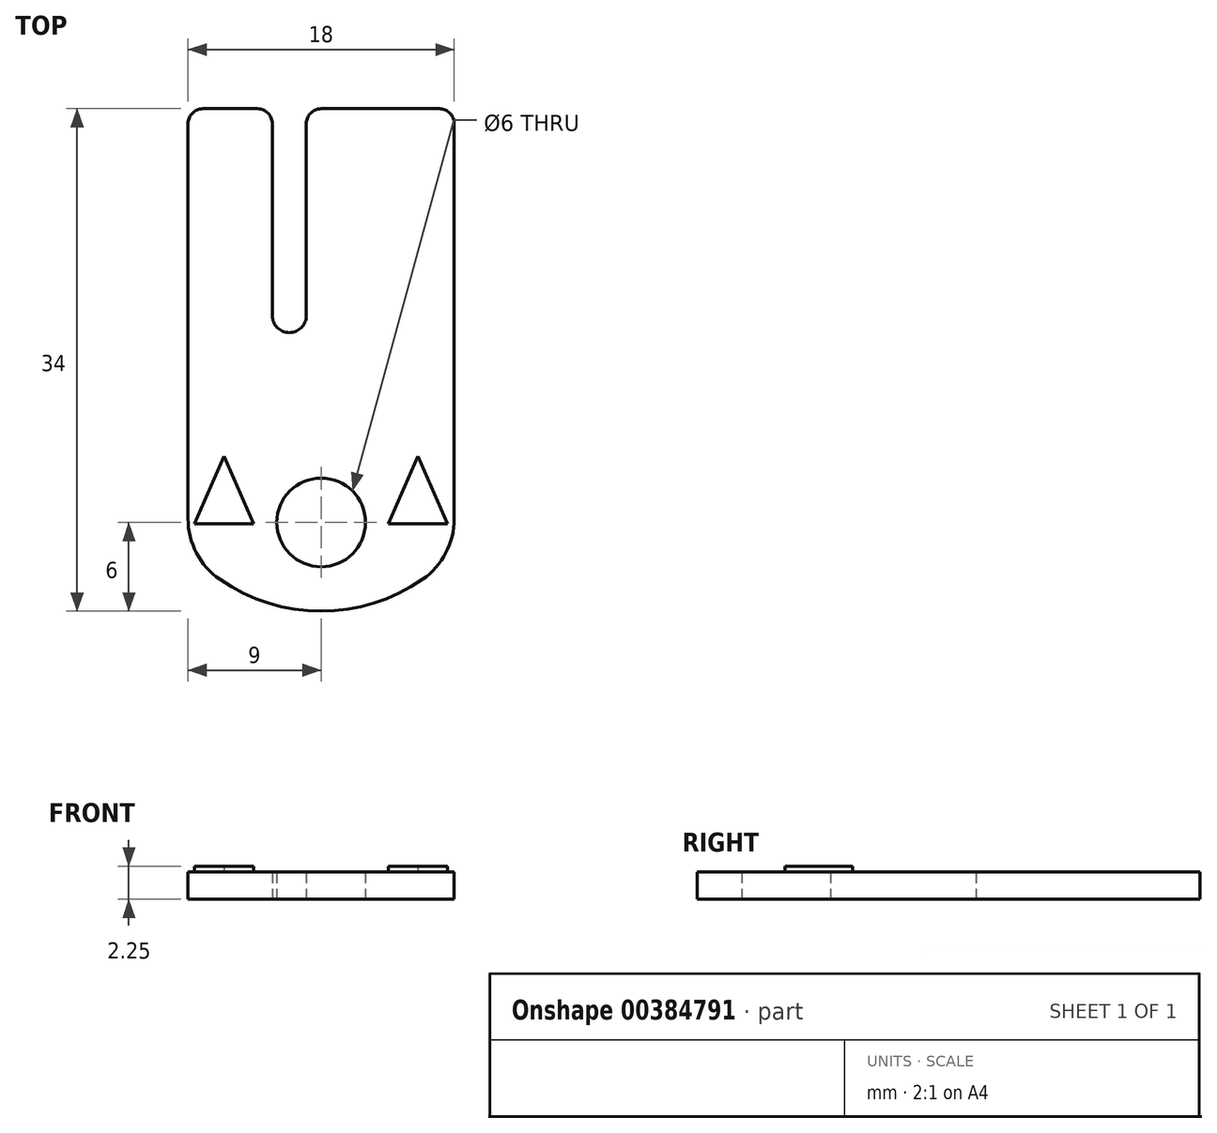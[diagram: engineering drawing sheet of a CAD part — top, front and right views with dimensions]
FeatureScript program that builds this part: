
annotation { "Feature Type Name" : "Feature", "Feature Type Description" : "" }
export const myFeature = defineFeature(function(context is Context, id is Id, definition is map)
    precondition{}
    {
        {
            var Q0;
            Q0=qCreatedBy(makeId("Top.planeOp"),FACE);
            var sketch = newSketch(context, id + "F0", { "sketchPlane" : qUnion([Q0])});
            skLineSegment(sketch, "E0.top", {"start": v(1, 22) * mm, "end": v(4.7, 22) * mm});
            skLineSegment(sketch, "E0.left", {"start": v(0, 1) * mm, "end": v(0, 21) * mm});
            skLineSegment(sketch, "E0.right", {"start": v(18, 1) * mm, "end": v(18, 21) * mm});
            skArc(sketch, "E1", {"start": v(2.14, -9.85) * mm, "mid": v(9, -12) * mm, "end": v(15.86, -9.85) * mm});
            skPoint(sketch, "E2.visualSharp", {"position": v(18, 22) * mm});
            skArc(sketch, "E2.filletArc", {"start": v(18, 21) * mm, "mid": v(17.7, 21.7) * mm, "end": v(17, 22) * mm});
            skPoint(sketch, "E3.visualSharp", {"position": v(0, 22) * mm});
            skArc(sketch, "E3.filletArc", {"start": v(1, 22) * mm, "mid": v(0.3, 21.7) * mm, "end": v(0, 21) * mm});
            skPoint(sketch, "E4.visualSharp", {"position": v(-3, 0) * mm});
            skPoint(sketch, "E5.visualSharp", {"position": v(21, 0) * mm});
            skPoint(sketch, "E6.visualSharp", {"position": v(18, 0) * mm});
            skPoint(sketch, "E7.visualSharp", {"position": v(0, 0) * mm});
            skLineSegment(sketch, "E8", {"start": v(5.7, 21) * mm, "end": v(5.7, 8) * mm});
            skLineSegment(sketch, "E9", {"start": v(8, 8) * mm, "end": v(8, 21) * mm});
            skArc(sketch, "E10", {"start": v(5.7, 8) * mm, "mid": v(6.85, 6.85) * mm, "end": v(8, 8) * mm});
            skLineSegment(sketch, "E11.trimOffspring", {"start": v(9, 22) * mm, "end": v(17, 22) * mm});
            skCircle(sketch, "E12", {"center": v(9, -6) * mm, "radius": 3 * mm});
            skPoint(sketch, "E12.centerSnap0", {"position": v(9, -12) * mm});
            skPoint(sketch, "E13.visualSharp", {"position": v(5.7, 22) * mm});
            skArc(sketch, "E13.filletArc", {"start": v(5.7, 21) * mm, "mid": v(5.4, 21.7) * mm, "end": v(4.7, 22) * mm});
            skPoint(sketch, "E14.visualSharp", {"position": v(8, 22) * mm});
            skArc(sketch, "E14.filletArc", {"start": v(9, 22) * mm, "mid": v(8.3, 21.7) * mm, "end": v(8, 21) * mm});
            skLineSegment(sketch, "E15", {"start": v(18, 1) * mm, "end": v(18, -5.74) * mm});
            skLineSegment(sketch, "E16", {"start": v(0, 1) * mm, "end": v(0, -5.74) * mm});
            skPoint(sketch, "E17.visualSharp", {"position": v(0, -7.94) * mm});
            skArc(sketch, "E17.filletArc", {"start": v(0, -5.74) * mm, "mid": v(0.57, -8.06) * mm, "end": v(2.14, -9.85) * mm});
            skPoint(sketch, "E18.visualSharp", {"position": v(18, -7.94) * mm});
            skArc(sketch, "E18.filletArc", {"start": v(15.86, -9.85) * mm, "mid": v(17.43, -8.06) * mm, "end": v(18, -5.74) * mm});
            skSolve(sketch);
        }
        {
            var Q0;
            Q0 = qSketchRegion(id + "F0", true);
            extrude(context, id + "F1", {"entities" : qUnion([Q0]), "depth" : 1.85 * mm});
        }
        {
            var Q0;
            Q0=makeQuery(id+"F1.opExtrude","CAP_FACE",FACE,{"disambiguationData":[OSD([sQuery(id+"F0.wireOp",EDGE,"E0.top"),sQuery(id+"F0.wireOp",EDGE,"E0.left"),sQuery(id+"F0.wireOp",EDGE,"E0.right"),sQuery(id+"F0.wireOp",EDGE,"E1"),sQuery(id+"F0.wireOp",EDGE,"HsPN8c6q-kJPd-bA8U-ZaCK-iASUxXpfGAAi"),sQuery(id+"F0.wireOp",EDGE,"Gjcc5HDl-sNZp-f0TE-VZhq-E6EV8sQHwBPA"),sQuery(id+"F0.wireOp",EDGE,"E2.filletArc"),sQuery(id+"F0.wireOp",EDGE,"E3.filletArc"),sQuery(id+"F0.wireOp",EDGE,"E4.filletArc"),sQuery(id+"F0.wireOp",EDGE,"E5.filletArc"),sQuery(id+"F0.wireOp",EDGE,"E6.filletArc"),sQuery(id+"F0.wireOp",EDGE,"E7.filletArc"),sQuery(id+"F0.wireOp",EDGE,"E8"),sQuery(id+"F0.wireOp",EDGE,"E9"),sQuery(id+"F0.wireOp",EDGE,"E10"),sQuery(id+"F0.wireOp",EDGE,"E11.trimOffspring"),sQuery(id+"F0.wireOp",EDGE,"E12"),sQuery(id+"F0.wireOp",EDGE,"E13.filletArc"),sQuery(id+"F0.wireOp",EDGE,"E14.filletArc")])],"isStart":false});
            var sketch = newSketch(context, id + "F2", { "sketchPlane" : qUnion([Q0])});
            skLineSegment(sketch, "E19", {"start": v(0.44, -6.08) * mm, "end": v(4.44, -6.08) * mm});
            skLineSegment(sketch, "E20", {"start": v(4.44, -6.08) * mm, "end": v(2.44, -1.5) * mm});
            skLineSegment(sketch, "E21", {"start": v(2.44, -1.5) * mm, "end": v(0.44, -6.08) * mm});
            skLineSegment(sketch, "E22", {"start": v(13.56, -6.08) * mm, "end": v(17.56, -6.08) * mm});
            skLineSegment(sketch, "E23", {"start": v(17.56, -6.08) * mm, "end": v(15.56, -1.5) * mm});
            skLineSegment(sketch, "E24", {"start": v(15.56, -1.5) * mm, "end": v(13.56, -6.08) * mm});
            skSolve(sketch);
        }
        {
            var Q0;
            Q0 = qSketchRegion(id + "F2", true);
            extrude(context, id + "F3", {"entities" : qUnion([Q0]), "operationType" : NewBodyOperationType.ADD, "depth" : .4 * mm});
        }
    });
